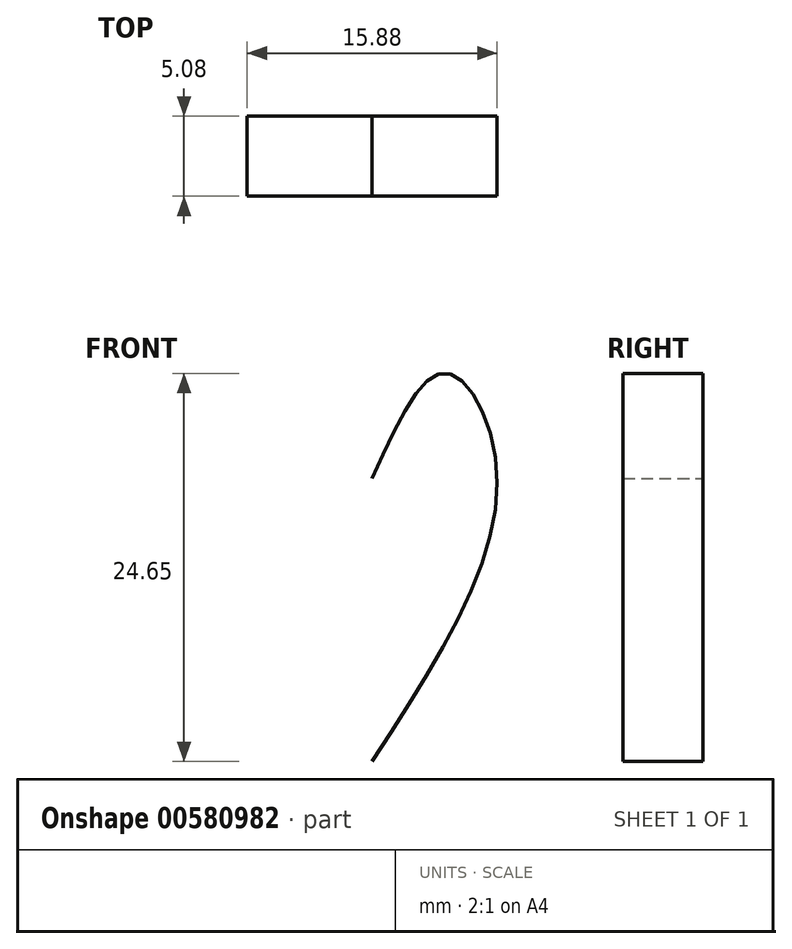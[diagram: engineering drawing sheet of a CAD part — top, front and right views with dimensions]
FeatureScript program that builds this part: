
annotation { "Feature Type Name" : "Feature", "Feature Type Description" : "" }
export const myFeature = defineFeature(function(context is Context, id is Id, definition is map)
    precondition{}
    {
        {
            var Q0;
            Q0=qCreatedBy(makeId("Front.planeOp"),FACE);
            var sketch = newSketch(context, id + "F0", { "sketchPlane" : qUnion([Q0])});
            skFitSpline(sketch, "E0", {"points": [v(0, 16.82) * mm, v(-4.63, 23.5) * mm, v(-7.94, 16.82) * mm, v(0, -1.14) * mm], "startDerivative": vector(-15.83, 35.52) * mm, "endDerivative": vector(27.36, -41.99) * mm});
            skFitSpline(sketch, "E1.MirrorCS", {"points": [v(0, 16.82) * mm, v(4.63, 23.5) * mm, v(7.94, 16.82) * mm, v(0, -1.14) * mm], "startDerivative": vector(15.83, 35.52) * mm, "endDerivative": vector(-27.36, -41.99) * mm});
            skSolve(sketch);
        }
        {
            var Q0;
            Q0=makeQuery(id+"F0.imprint","IMPRINT",FACE,{"disambiguationData":[TD([[makeQuery(id+"F0.imprint","IMPRINT",EDGE,{"derivedFrom":sQuery(id+"F0.wireOp",EDGE,"E0")}),1.0]])]});
            extrude(context, id + "F1", {"entities" : qUnion([Q0]), "depth" : 5.08 * mm, "offsetDistance" : 25.4 * mm});
        }
    });
